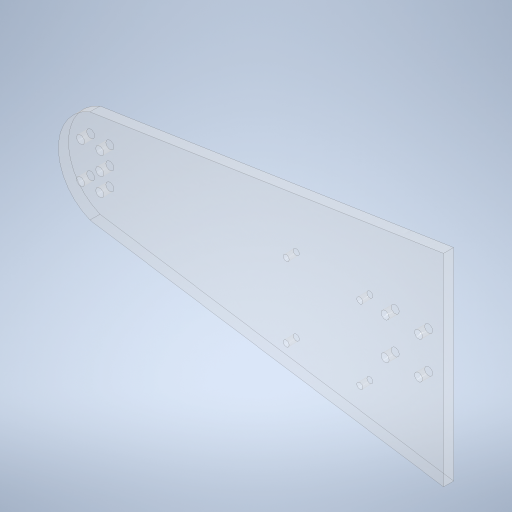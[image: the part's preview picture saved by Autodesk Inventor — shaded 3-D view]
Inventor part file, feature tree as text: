
AUTODESK INVENTOR PART (.ipt)
format: ipt  version: 2023.1 (Build 271208000, 208)  size: 304,640 bytes
history: native  units: in
note: dims shown in document units (in); Inventor stores cm internally (conversion verified against a paired STEP export)
features: reference x5, other x3, extrude x1, hole x1, sketch x1
ambient origin geometry x8: Origin, YZ Plane, XZ Plane, XY Plane, X Axis, Y Axis, Z Axis, Center Point
bodies: Solid1 (feature_tree)
feature tree (11):
  extrude  "Extrusion1"  Depth=0.9843in
  hole  "Hole1"  [1 undecoded]
  reference  "Reference2"
  reference  "Reference8"
  reference  "Reference9"
  reference  "Reference10"
  reference  "Reference11"
  sketch  "Sketch2"  dims[d0=3.937in d1=1.9685in d4=0.1969in d5=0.0in d7=0.1339in d8=0.1181in d9=0.0in d10=0.1181in d11=1.4409in d12=0.8504in d14=0.1181in d15=0.2362in d16=0.1575in d17=0.0787in d18=90.0deg d19=0.315in d20=0.8108in d24=1.9685in d25=0.9843in d27=0.0in d28=0.3543in d29=0.3543in d30=0.1575in d31=0.0in d32=0.0in d33=6.5146in]
  other  "Ensamble.iam"
  other  "base:1"
  other  "SoporteUnion:1"
note: 1 required parameter value undecoded (feature->parameter linkage not recoverable at this tier; creation-order binding heuristic only, values carry confidence <= 0.55)
